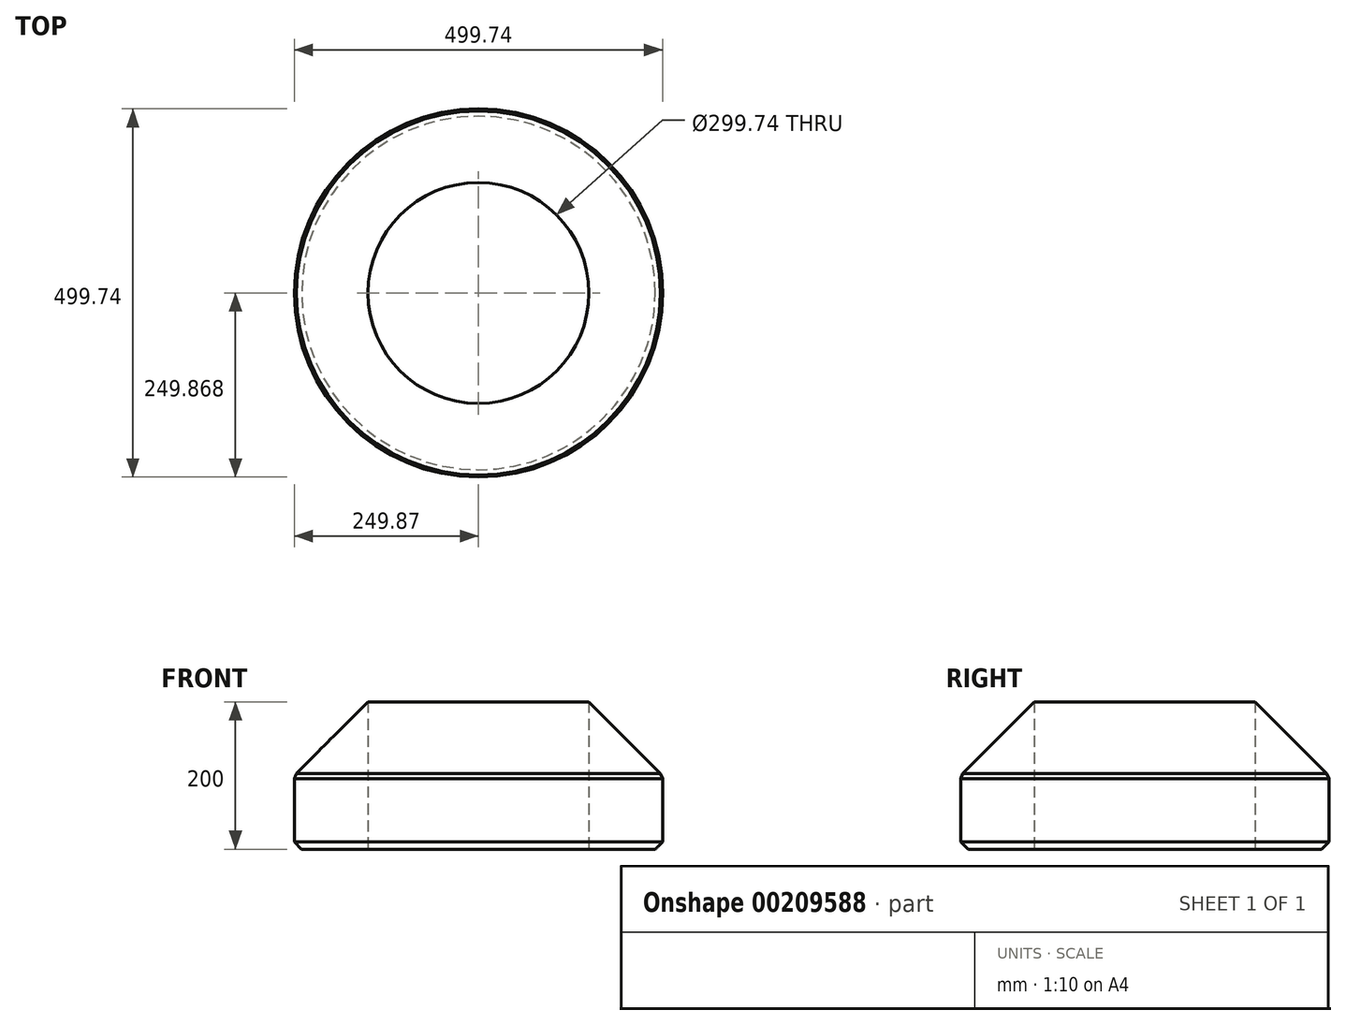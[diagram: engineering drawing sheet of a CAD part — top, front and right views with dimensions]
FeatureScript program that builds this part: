
annotation { "Feature Type Name" : "Feature", "Feature Type Description" : "" }
export const myFeature = defineFeature(function(context is Context, id is Id, definition is map)
    precondition{}
    {
        {
            var Q0;
            Q0=qCreatedBy(makeId("Front.planeOp"),FACE);
            var sketch = newSketch(context, id + "F0", { "sketchPlane" : qUnion([Q0])});
            skLineSegment(sketch, "E0", {"start": v(-14.36, 25.63) * mm, "end": v(10.08, -18) * mm});
            skLineSegment(sketch, "E1", {"start": v(10.08, -18) * mm, "end": v(17.44, 31.46) * mm});
            skLineSegment(sketch, "E2", {"start": v(17.44, 31.46) * mm, "end": v(-21.42, 0) * mm});
            skLineSegment(sketch, "E3", {"start": v(-21.42, 0) * mm, "end": v(28.58, 0) * mm});
            skLineSegment(sketch, "E4", {"start": v(28.58, 0) * mm, "end": v(-14.36, 25.63) * mm});
            skPoint(sketch, "E5", {"position": v(0, 0) * mm});
            skPoint(sketch, "E6", {"position": v(-6.68, 11.93) * mm});
            skPoint(sketch, "E7", {"position": v(17.44, 31.46) * mm});
            skSolve(sketch);
        }
        {
            var Q0;
            Q0 = qSketchRegion(id + "F0", true);
            extrude(context, id + "F1", {"entities" : qUnion([Q0]), "depth" : 25 * mm, "hasDraft" : true, "draftAngle" : 5 * degree, "hasSecondDirection" : true, "secondDirectionOppositeDirection" : true, "secondDirectionDepth" : 20 * mm});
        }
        {
            var Q0;
            {var subQ0=sQuery(id+"F0.wireOp",EDGE,"E4");Q0=makeQuery(id+"F1.*.split.splitOp","SPLIT",FACE,{"derivedFrom":makeQuery(id+"F1.opExtrude","SWEPT_FACE",FACE,{"disambiguationData":[OSD([subQ0]),TDD([makeQuery(id+"F0.imprint","IMPRINT",EDGE,{"disambiguationData":[TD([[makeQuery(id+"F0.imprint","INTERSECT",VERTEX,{"derivedFrom":[sQuery(id+"F0.wireOp",EDGE,"E0"),subQ0]}),1.0]])],"derivedFrom":subQ0})])]})});}
            var sketch = newSketch(context, id + "F2", { "sketchPlane" : qUnion([Q0])});
            skPoint(sketch, "E8", {"position": v(-20.07, -15.34) * mm});
            skPoint(sketch, "E9", {"position": v(-20.3, -13.34) * mm});
            skCircle(sketch, "E10", {"center": v(-20.07, -15.34) * mm, "radius": 5.85 * mm});
            skPoint(sketch, "E11", {"position": v(-17.13, -2.17) * mm});
            skSolve(sketch);
        }
        {
            var Q0;
            Q0 = qSketchRegion(id + "F2", true);
            extrude(context, id + "F3", {"entities" : qUnion([Q0]), "operationType" : NewBodyOperationType.REMOVE, "endBound" : BoundingType.UP_TO_NEXT, "oppositeDirection" : true, "depth" : 25 * mm, "hasDraft" : true, "draftAngle" : 3 * degree});
        }
        {
            var Q0;
            Q0=qCreatedBy(makeId("Right.planeOp"),FACE);
            var sketch = newSketch(context, id + "F4", { "sketchPlane" : qUnion([Q0])});
            skLineSegment(sketch, "E12.bottom", {"start": v(50, 50) * mm, "end": v(-50, 50) * mm});
            skLineSegment(sketch, "E12.top", {"start": v(50, -50) * mm, "end": v(-50, -50) * mm});
            skLineSegment(sketch, "E12.left", {"start": v(50, 50) * mm, "end": v(50, -50) * mm});
            skLineSegment(sketch, "E12.right", {"start": v(-50, 50) * mm, "end": v(-50, -50) * mm});
            skPoint(sketch, "E12.middle", {"position": v(0, 0) * mm});
            skLineSegment(sketch, "E13", {"start": v(-50, 50) * mm, "end": v(-50, 150) * mm});
            skLineSegment(sketch, "E14", {"start": v(-50, 150) * mm, "end": v(50, 50) * mm});
            skLineSegment(sketch, "E15", {"start": v(-50, -50) * mm, "end": v(-50, 177.73) * mm, "construction": true});
            skLineSegment(sketch, "E16", {"start": v(-50, -50) * mm, "end": v(-199.87, -50) * mm, "construction": true});
            skLineSegment(sketch, "E17", {"start": v(-199.87, -50) * mm, "end": v(-199.87, 177.1) * mm, "construction": true});
            skSolve(sketch);
        }
        {
            var Q0;
            Q0 = qSketchRegion(id + "F4", true);
            var Q1;
            Q1=sQuery(id+"F4.wireOp",EDGE,"E17");
            revolve(context, id + "F5", {"operationType" : NewBodyOperationType.ADD, "entities" : qUnion([Q0]), "axis" : qUnion([Q1]), "revolveType" : RevolveType.FULL});
        }
        {
            var Q0;
            Q0=makeQuery(id+"F5.opRevolve","SWEPT_FACE",FACE,{"disambiguationData":[OSD([sQuery(id+"F4.wireOp",EDGE,"E12.left")])]});
            chamfer(context, id + "F6", {"entities" : qUnion([Q0]), "width" : 10 * mm, "tangentPropagation" : true});
        }
    });
